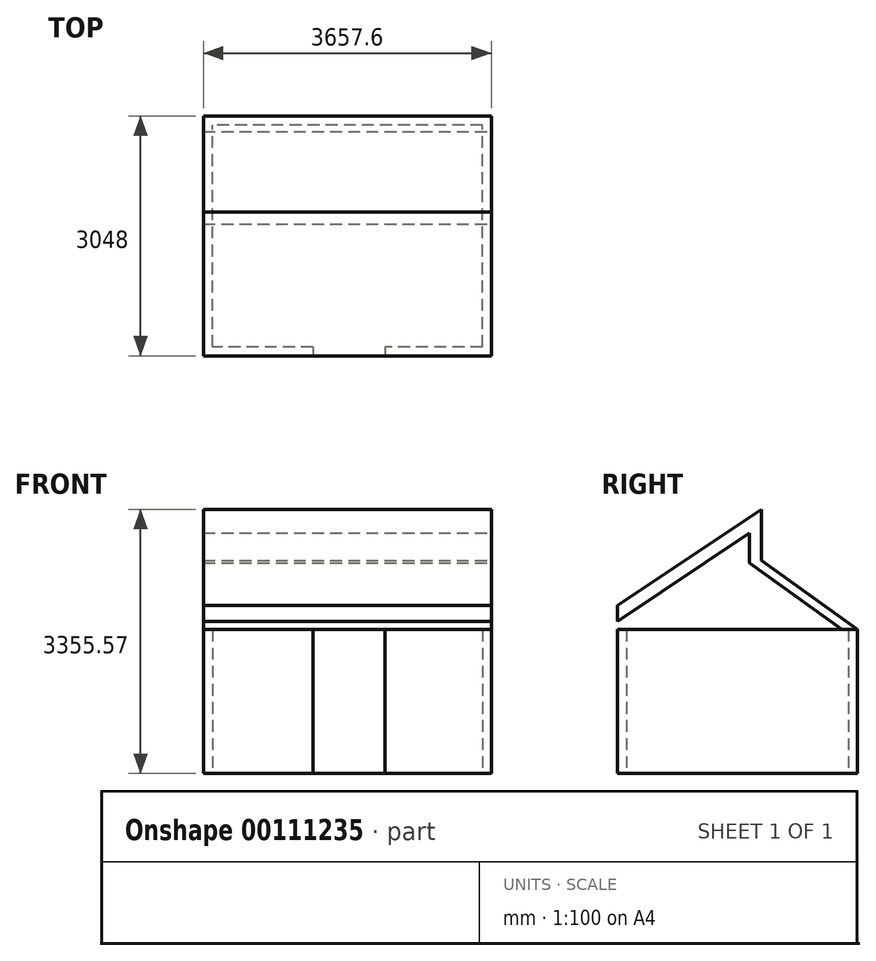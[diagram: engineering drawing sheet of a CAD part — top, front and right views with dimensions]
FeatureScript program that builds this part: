
annotation { "Feature Type Name" : "Feature", "Feature Type Description" : "" }
export const myFeature = defineFeature(function(context is Context, id is Id, definition is map)
    precondition{}
    {
        {
            var Q0;
            Q0=qCreatedBy(makeId("Top.planeOp"),FACE);
            var sketch = newSketch(context, id + "F0", { "sketchPlane" : qUnion([Q0])});
            skLineSegment(sketch, "E0.bottom", {"start": v(1828.8, -1524) * mm, "end": v(-1828.8, -1524) * mm});
            skLineSegment(sketch, "E0.top", {"start": v(1828.8, 1524) * mm, "end": v(-1828.8, 1524) * mm});
            skLineSegment(sketch, "E0.left", {"start": v(1828.8, -1524) * mm, "end": v(1828.8, 1524) * mm});
            skLineSegment(sketch, "E0.right", {"start": v(-1828.8, -1524) * mm, "end": v(-1828.8, 1524) * mm});
            skPoint(sketch, "E0.middle", {"position": v(0, 0) * mm});
            skLineSegment(sketch, "E1.bottom", {"start": v(1714.5, -1409.7) * mm, "end": v(-1714.5, -1409.7) * mm});
            skLineSegment(sketch, "E1.top", {"start": v(1714.5, 1409.7) * mm, "end": v(-1714.5, 1409.7) * mm});
            skLineSegment(sketch, "E1.left", {"start": v(1714.5, -1409.7) * mm, "end": v(1714.5, 1409.7) * mm});
            skLineSegment(sketch, "E1.right", {"start": v(-1714.5, -1409.7) * mm, "end": v(-1714.5, 1409.7) * mm});
            skSolve(sketch);
        }
        {
            var Q0;
            Q0 = qSketchRegion(id + "F0", true);
            extrude(context, id + "F1", {"entities" : qUnion([Q0]), "depth" : 1828.8 * mm});
        }
        {
            var Q0;
            Q0=makeQuery(id+"F1.opExtrude","SWEPT_FACE",FACE,{"disambiguationData":[OSD([sQuery(id+"F0.wireOp",EDGE,"E0.left")])]});
            var sketch = newSketch(context, id + "F2", { "sketchPlane" : qUnion([Q0])});
            skPoint(sketch, "E2", {"position": v(1524, 863.6) * mm});
            skPoint(sketch, "E3", {"position": v(0, 1828.8) * mm});
            skLineSegment(sketch, "E4", {"start": v(-1524, 1828.8) * mm, "end": v(-1524, 3642.83) * mm, "construction": true});
            skLineSegment(sketch, "E5", {"start": v(-1350.61, 1828.8) * mm, "end": v(1570.13, 1828.8) * mm, "construction": true});
            skLineSegment(sketch, "E6", {"start": v(1524, 863.6) * mm, "end": v(914.4, 863.6) * mm});
            skLineSegment(sketch, "E7", {"start": v(304.8, 2706.64) * mm, "end": v(1524, 1828.8) * mm});
            skLineSegment(sketch, "E8", {"start": v(304.8, 3355.57) * mm, "end": v(304.8, 2706.64) * mm});
            skLineSegment(sketch, "E9", {"start": v(-1524, 2133.6) * mm, "end": v(304.8, 3355.57) * mm});
            skLineSegment(sketch, "E10", {"start": v(-1524, 1935) * mm, "end": v(152.4, 3055.13) * mm});
            skLineSegment(sketch, "E11", {"start": v(152.4, 3055.13) * mm, "end": v(152.4, 2674.36) * mm});
            skLineSegment(sketch, "E12", {"start": v(152.4, 2674.36) * mm, "end": v(1326.76, 1828.8) * mm});
            skLineSegment(sketch, "E13", {"start": v(1326.76, 1828.8) * mm, "end": v(1524, 1828.8) * mm});
            skLineSegment(sketch, "E14", {"start": v(-1524, 2133.6) * mm, "end": v(-1524, 1935) * mm});
            skSolve(sketch);
        }
        {
            var Q0;
            Q0 = qSketchRegion(id + "F2", true);
            extrude(context, id + "F3", {"entities" : qUnion([Q0]), "oppositeDirection" : true, "depth" : 3657.6 * mm});
        }
        {
            var Q0;
            Q0=makeQuery(id+"F1.opExtrude","SWEPT_FACE",FACE,{"disambiguationData":[OSD([sQuery(id+"F0.wireOp",EDGE,"E0.bottom")])]});
            var sketch = newSketch(context, id + "F4", { "sketchPlane" : qUnion([Q0])});
            skLineSegment(sketch, "E15.bottom", {"start": v(-438.11, 0) * mm, "end": v(476.29, 0) * mm});
            skLineSegment(sketch, "E15.top", {"start": v(-438.11, 1828.8) * mm, "end": v(476.29, 1828.8) * mm});
            skLineSegment(sketch, "E15.left", {"start": v(-438.11, 0) * mm, "end": v(-438.11, 1828.8) * mm});
            skLineSegment(sketch, "E15.right", {"start": v(476.29, 0) * mm, "end": v(476.29, 1828.8) * mm});
            skSolve(sketch);
        }
        {
            var Q0;
            Q0 = qSketchRegion(id + "F4", true);
            extrude(context, id + "F5", {"entities" : qUnion([Q0]), "operationType" : NewBodyOperationType.REMOVE, "endBound" : BoundingType.UP_TO_NEXT, "oppositeDirection" : true, "depth" : 25.4 * mm});
        }
    });
